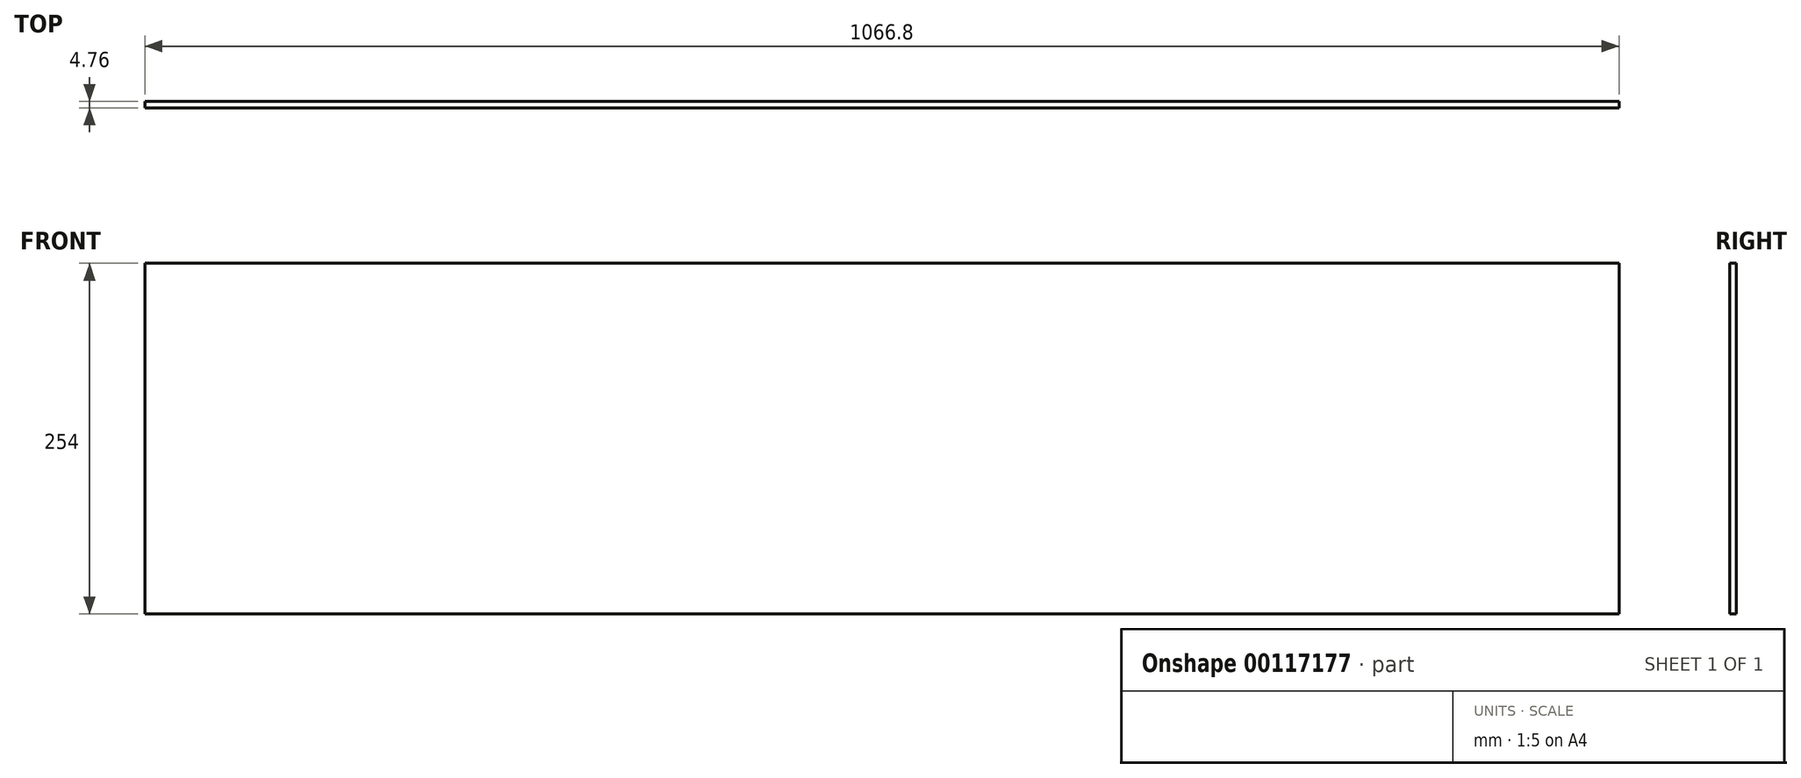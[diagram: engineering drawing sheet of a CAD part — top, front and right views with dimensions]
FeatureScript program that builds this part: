
annotation { "Feature Type Name" : "Feature", "Feature Type Description" : "" }
export const myFeature = defineFeature(function(context is Context, id is Id, definition is map)
    precondition{}
    {
        {
            var Q0;
            Q0=qCreatedBy(makeId("Front.planeOp"),FACE);
            var sketch = newSketch(context, id + "F0", { "sketchPlane" : qUnion([Q0])});
            skLineSegment(sketch, "E0.bottom", {"start": v(-598.25, 148.4) * mm, "end": v(468.55, 148.4) * mm});
            skLineSegment(sketch, "E0.top", {"start": v(-598.25, -105.6) * mm, "end": v(468.55, -105.6) * mm});
            skLineSegment(sketch, "E0.left", {"start": v(-598.25, 148.4) * mm, "end": v(-598.25, -105.6) * mm});
            skLineSegment(sketch, "E0.right", {"start": v(468.55, 148.4) * mm, "end": v(468.55, -105.6) * mm});
            skSolve(sketch);
        }
        {
            var Q0;
            Q0=makeQuery(id+"F0.imprint","IMPRINT",FACE,{"disambiguationData":[TD([[makeQuery(id+"F0.imprint","IMPRINT",EDGE,{"derivedFrom":sQuery(id+"F0.wireOp",EDGE,"E0.bottom")}),-1.0]])]});
            extrude(context, id + "F1", {"entities" : qUnion([Q0]), "depth" : 4.76 * mm});
        }
    });
